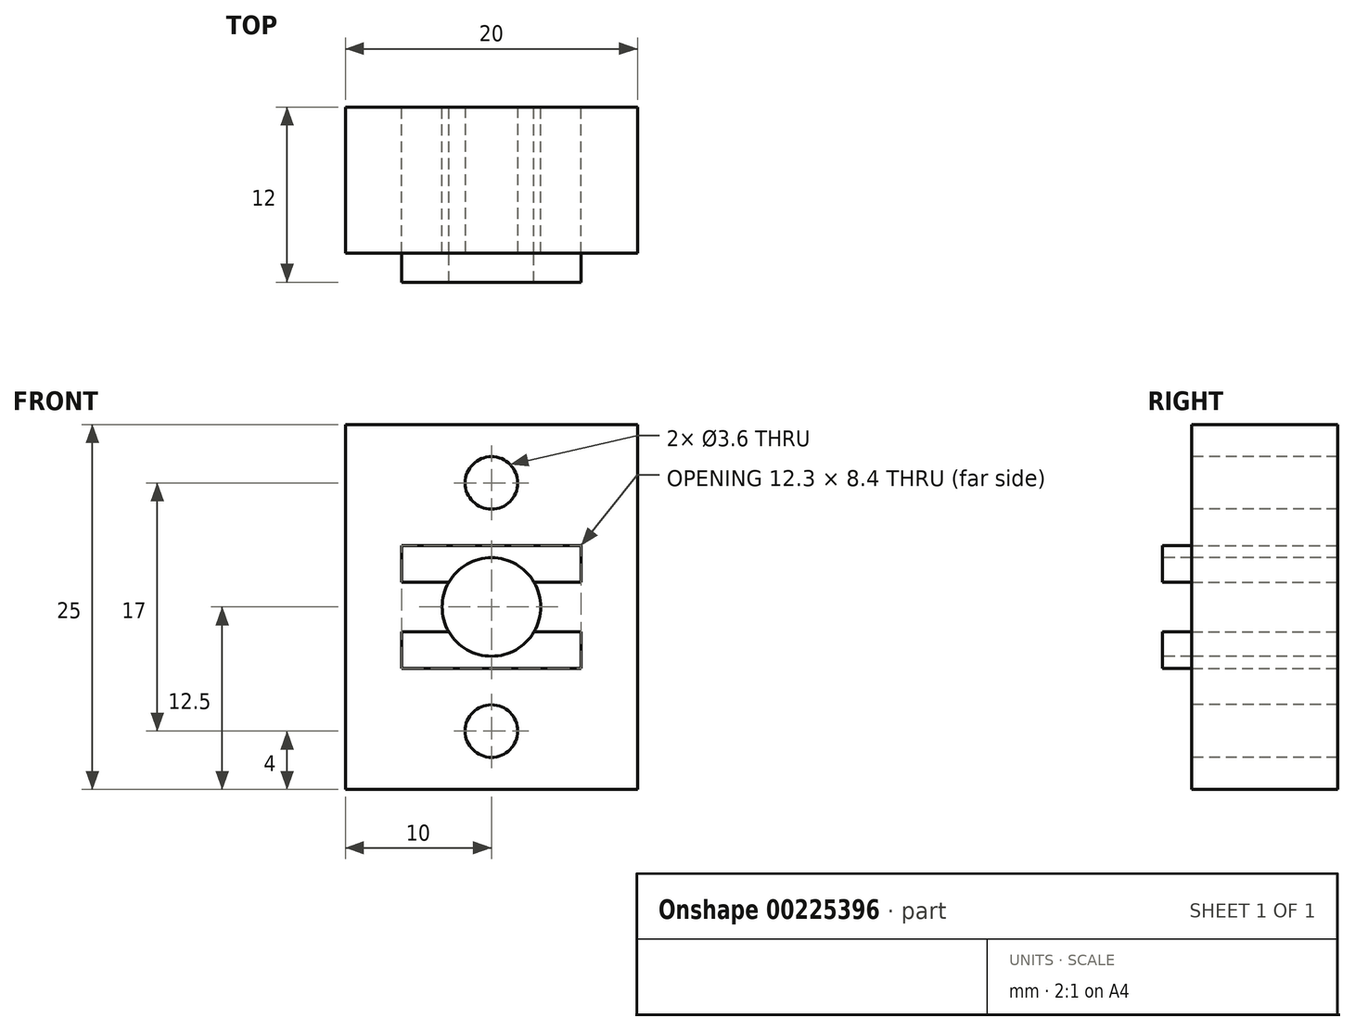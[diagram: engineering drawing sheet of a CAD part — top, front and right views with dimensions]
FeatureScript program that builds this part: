
annotation { "Feature Type Name" : "Feature", "Feature Type Description" : "" }
export const myFeature = defineFeature(function(context is Context, id is Id, definition is map)
    precondition{}
    {
        {
            var Q0;
            Q0=qCreatedBy(makeId("Front.planeOp"),FACE);
            var sketch = newSketch(context, id + "F0", { "sketchPlane" : qUnion([Q0])});
            skLineSegment(sketch, "E0.bottom", {"start": v(-5, 12.5) * mm, "end": v(5, 12.5) * mm, "construction": true});
            skLineSegment(sketch, "E0.top", {"start": v(-5, -12.5) * mm, "end": v(5, -12.5) * mm, "construction": true});
            skLineSegment(sketch, "E0.left", {"start": v(-5, 12.5) * mm, "end": v(-5, -12.5) * mm, "construction": true});
            skLineSegment(sketch, "E0.right", {"start": v(5, 12.5) * mm, "end": v(5, -12.5) * mm, "construction": true});
            skPoint(sketch, "E0.middle", {"position": v(0, 0) * mm});
            skCircle(sketch, "E1", {"center": v(5, 0) * mm, "radius": 3.17 * mm, "construction": true});
            skCircle(sketch, "E2", {"center": v(2.05, 2.95) * mm, "radius": 1 * mm, "construction": true});
            skCircle(sketch, "E3", {"center": v(2.05, -2.95) * mm, "radius": 1 * mm, "construction": true});
            skLineSegment(sketch, "E4", {"start": v(5, 0) * mm, "end": v(2.05, 2.95) * mm, "construction": true});
            skLineSegment(sketch, "E5", {"start": v(2.05, -2.95) * mm, "end": v(5, 0) * mm, "construction": true});
            skLineSegment(sketch, "E6.bottom", {"start": v(-1.15, 4.2) * mm, "end": v(3.25, 4.2) * mm, "construction": true});
            skLineSegment(sketch, "E6.top", {"start": v(-1.15, 1.7) * mm, "end": v(3.25, 1.7) * mm, "construction": true});
            skLineSegment(sketch, "E6.left", {"start": v(-1.15, 4.2) * mm, "end": v(-1.15, 1.7) * mm, "construction": true});
            skLineSegment(sketch, "E6.right", {"start": v(3.25, 4.2) * mm, "end": v(3.25, 1.7) * mm, "construction": true});
            skPoint(sketch, "E6.middle", {"position": v(1.05, 2.95) * mm});
            skLineSegment(sketch, "E7.MirrorCS", {"start": v(-1.15, -1.7) * mm, "end": v(3.25, -1.7) * mm, "construction": true});
            skLineSegment(sketch, "E8.MirrorCS", {"start": v(-1.15, -4.2) * mm, "end": v(-1.15, -1.7) * mm, "construction": true});
            skLineSegment(sketch, "E9.MirrorCS", {"start": v(-1.15, -4.2) * mm, "end": v(3.25, -4.2) * mm, "construction": true});
            skLineSegment(sketch, "E10.MirrorCS", {"start": v(3.25, -4.2) * mm, "end": v(3.25, -1.7) * mm, "construction": true});
            skLineSegment(sketch, "E11", {"start": v(-1.15, 4.2) * mm, "end": v(5, 4.2) * mm});
            skLineSegment(sketch, "E12", {"start": v(5, 12.5) * mm, "end": v(5, 4.2) * mm});
            skLineSegment(sketch, "E13", {"start": v(5, 12.5) * mm, "end": v(-5, 12.5) * mm});
            skLineSegment(sketch, "E14", {"start": v(-5, 12.5) * mm, "end": v(-5, -12.5) * mm});
            skLineSegment(sketch, "E15", {"start": v(-5, -12.5) * mm, "end": v(5, -12.5) * mm});
            skArc(sketch, "E16", {"start": v(2.09, 1.7) * mm, "mid": v(1.62, 0) * mm, "end": v(2.09, -1.7) * mm});
            skLineSegment(sketch, "E17", {"start": v(-1.15, 4.2) * mm, "end": v(-1.15, 1.7) * mm});
            skLineSegment(sketch, "E18", {"start": v(-1.15, 1.7) * mm, "end": v(2.09, 1.7) * mm});
            skLineSegment(sketch, "E19", {"start": v(-1.15, -1.7) * mm, "end": v(2.09, -1.7) * mm});
            skLineSegment(sketch, "E20", {"start": v(-1.15, -1.7) * mm, "end": v(-1.15, -4.2) * mm});
            skLineSegment(sketch, "E21", {"start": v(-1.15, -4.2) * mm, "end": v(5, -4.2) * mm});
            skLineSegment(sketch, "E22", {"start": v(5, -4.2) * mm, "end": v(5, -12.5) * mm});
            skCircle(sketch, "E23", {"center": v(0.05, 2.95) * mm, "radius": 1 * mm, "construction": true});
            skLineSegment(sketch, "E24", {"start": v(5, 0) * mm, "end": v(5, 15.82) * mm, "construction": true});
            skLineSegment(sketch, "E25", {"start": v(5, 15.82) * mm, "end": v(5, -17.9) * mm, "construction": true});
            skLineSegment(sketch, "E26.MirrorCS", {"start": v(11.15, 1.7) * mm, "end": v(7.91, 1.7) * mm});
            skLineSegment(sketch, "E27.MirrorCS", {"start": v(15, -12.5) * mm, "end": v(5, -12.5) * mm});
            skLineSegment(sketch, "E28.MirrorCS", {"start": v(5, 12.5) * mm, "end": v(15, 12.5) * mm});
            skLineSegment(sketch, "E29.MirrorCS", {"start": v(11.15, 4.2) * mm, "end": v(11.15, 1.7) * mm});
            skLineSegment(sketch, "E30.MirrorCS", {"start": v(15, 12.5) * mm, "end": v(15, -12.5) * mm});
            skLineSegment(sketch, "E31.MirrorCS", {"start": v(11.15, -1.7) * mm, "end": v(11.15, -4.2) * mm});
            skLineSegment(sketch, "E32.MirrorCS", {"start": v(11.15, -1.7) * mm, "end": v(7.91, -1.7) * mm});
            skLineSegment(sketch, "E33.MirrorCS", {"start": v(15, -12.5) * mm, "end": v(5, -12.5) * mm, "construction": true});
            skLineSegment(sketch, "E34.MirrorCS", {"start": v(11.15, -4.2) * mm, "end": v(6.75, -4.2) * mm, "construction": true});
            skLineSegment(sketch, "E35.MirrorCS", {"start": v(11.15, 4.2) * mm, "end": v(11.15, 1.7) * mm, "construction": true});
            skLineSegment(sketch, "E36.MirrorCS", {"start": v(6.75, -4.2) * mm, "end": v(6.75, -1.7) * mm, "construction": true});
            skLineSegment(sketch, "E37.MirrorCS", {"start": v(11.15, 4.2) * mm, "end": v(5, 4.2) * mm});
            skPoint(sketch, "E38.MirrorP", {"position": v(10, 0) * mm});
            skCircle(sketch, "E39.MirrorC", {"center": v(9.95, 2.95) * mm, "radius": 1 * mm, "construction": true});
            skLineSegment(sketch, "E40.MirrorCS", {"start": v(15, 12.5) * mm, "end": v(15, -12.5) * mm, "construction": true});
            skCircle(sketch, "E41.MirrorC", {"center": v(7.95, 2.95) * mm, "radius": 1 * mm, "construction": true});
            skLineSegment(sketch, "E42.MirrorCS", {"start": v(11.15, 1.7) * mm, "end": v(6.75, 1.7) * mm, "construction": true});
            skLineSegment(sketch, "E43.MirrorCS", {"start": v(11.15, -4.2) * mm, "end": v(11.15, -1.7) * mm, "construction": true});
            skCircle(sketch, "E44.MirrorC", {"center": v(7.95, -2.95) * mm, "radius": 1 * mm, "construction": true});
            skLineSegment(sketch, "E45.MirrorCS", {"start": v(11.15, -1.7) * mm, "end": v(6.75, -1.7) * mm, "construction": true});
            skArc(sketch, "E46.MirrorCS", {"start": v(7.91, 1.7) * mm, "mid": v(8.37, 0) * mm, "end": v(7.91, -1.7) * mm});
            skLineSegment(sketch, "E47.MirrorCS", {"start": v(6.75, 4.2) * mm, "end": v(6.75, 1.7) * mm, "construction": true});
            skLineSegment(sketch, "E48.MirrorCS", {"start": v(7.95, -2.95) * mm, "end": v(5, 0) * mm, "construction": true});
            skLineSegment(sketch, "E49.MirrorCS", {"start": v(11.15, -4.2) * mm, "end": v(5, -4.2) * mm});
            skPoint(sketch, "E50.MirrorP", {"position": v(8.95, 2.95) * mm});
            skLineSegment(sketch, "E51.MirrorCS", {"start": v(5, 0) * mm, "end": v(7.95, 2.95) * mm, "construction": true});
            skLineSegment(sketch, "E52.MirrorCS", {"start": v(15, 12.5) * mm, "end": v(5, 12.5) * mm, "construction": true});
            skLineSegment(sketch, "E53.MirrorCS", {"start": v(11.15, 4.2) * mm, "end": v(6.75, 4.2) * mm, "construction": true});
            skSolve(sketch);
        }
        {
            var Q0;
            Q0=makeQuery(id+"F0.imprint","IMPRINT",FACE,{"disambiguationData":[TD([[makeQuery(id+"F0.imprint","IMPRINT",EDGE,{"derivedFrom":sQuery(id+"F0.wireOp",EDGE,"E11")}),1.0]])]});
            var Q1;
            Q1=makeQuery(id+"F0.imprint","IMPRINT",FACE,{"disambiguationData":[TD([[makeQuery(id+"F0.imprint","IMPRINT",EDGE,{"derivedFrom":sQuery(id+"F0.wireOp",EDGE,"E26.MirrorCS")}),1.0]])]});
            extrude(context, id + "F1", {"entities" : qUnion([Q0, Q1]), "endBound" : BoundingType.SYMMETRIC, "offsetDistance" : 25 * mm, "depth" : 10 * mm});
        }
        {
            var Q0;
            Q0=makeQuery(id+"F1.opExtrude","CAP_FACE",FACE,{"disambiguationData":[OSD([sQuery(id+"F0.wireOp",EDGE,"E11"),sQuery(id+"F0.wireOp",EDGE,"E13"),sQuery(id+"F0.wireOp",EDGE,"E14"),sQuery(id+"F0.wireOp",EDGE,"E15"),sQuery(id+"F0.wireOp",EDGE,"E16"),sQuery(id+"F0.wireOp",EDGE,"E17"),sQuery(id+"F0.wireOp",EDGE,"E18"),sQuery(id+"F0.wireOp",EDGE,"E19"),sQuery(id+"F0.wireOp",EDGE,"E20"),sQuery(id+"F0.wireOp",EDGE,"E21"),sQuery(id+"F0.wireOp",EDGE,"E26.MirrorCS"),sQuery(id+"F0.wireOp",EDGE,"E27.MirrorCS"),sQuery(id+"F0.wireOp",EDGE,"E28.MirrorCS"),sQuery(id+"F0.wireOp",EDGE,"E29.MirrorCS"),sQuery(id+"F0.wireOp",EDGE,"E30.MirrorCS"),sQuery(id+"F0.wireOp",EDGE,"E31.MirrorCS"),sQuery(id+"F0.wireOp",EDGE,"E32.MirrorCS"),sQuery(id+"F0.wireOp",EDGE,"E37.MirrorCS"),sQuery(id+"F0.wireOp",EDGE,"E46.MirrorCS"),sQuery(id+"F0.wireOp",EDGE,"E49.MirrorCS")])],"isStart":false});
            var sketch = newSketch(context, id + "F2", { "sketchPlane" : qUnion([Q0])});
            skPoint(sketch, "E54", {"position": v(5, 8.5) * mm});
            skPoint(sketch, "E54.positionSnap0", {"position": v(5, 4.2) * mm});
            skPoint(sketch, "E55", {"position": v(5, -8.5) * mm});
            skSolve(sketch);
        }
        {
            var Q0;
            Q0=sQuery(id+"F2.wireOp",VERTEX,"E54");
            var Q1;
            Q1=sQuery(id+"F2.wireOp",VERTEX,"E55");
            var Q2;
            Q2=makeQuery(id+"F1.opExtrude","SWEPT_BODY",BODY,{"disambiguationData":[OSD([sQuery(id+"F0.wireOp",EDGE,"E11"),sQuery(id+"F0.wireOp",EDGE,"E13"),sQuery(id+"F0.wireOp",EDGE,"E14"),sQuery(id+"F0.wireOp",EDGE,"E15"),sQuery(id+"F0.wireOp",EDGE,"E16"),sQuery(id+"F0.wireOp",EDGE,"E17"),sQuery(id+"F0.wireOp",EDGE,"E18"),sQuery(id+"F0.wireOp",EDGE,"E19"),sQuery(id+"F0.wireOp",EDGE,"E20"),sQuery(id+"F0.wireOp",EDGE,"E21"),sQuery(id+"F0.wireOp",EDGE,"E26.MirrorCS"),sQuery(id+"F0.wireOp",EDGE,"E27.MirrorCS"),sQuery(id+"F0.wireOp",EDGE,"E28.MirrorCS"),sQuery(id+"F0.wireOp",EDGE,"E29.MirrorCS"),sQuery(id+"F0.wireOp",EDGE,"E30.MirrorCS"),sQuery(id+"F0.wireOp",EDGE,"E31.MirrorCS"),sQuery(id+"F0.wireOp",EDGE,"E32.MirrorCS"),sQuery(id+"F0.wireOp",EDGE,"E37.MirrorCS"),sQuery(id+"F0.wireOp",EDGE,"E46.MirrorCS"),sQuery(id+"F0.wireOp",EDGE,"E49.MirrorCS")])]});
            hole(context, id + "F3", {"style" : HoleStyle.SIMPLE, "endStyle" : HoleEndStyle.BLIND, "standardTappedOrClearance" : lookupTablePath({ "fit" : "Loose", "standard" : "ISO", "size" : "M3", "type" : "Clearance" }), "standardBlindInLast" : lookupTablePath({ "fit" : "Loose", "standard" : "ISO", "engagement" : "75%", "pitch" : "0.5 mm", "size" : "M3", "type" : "Clearance & tapped" }), "holeDiameter" : 3.6 * mm, "majorDiameter" : 5 * mm, "holeDepth" : 35 * mm, "isTappedThrough" : true, "tappedDepth" : 12 * mm, "tapClearance" : 3, "startFromSketch" : true, "locations" : qUnion([Q0, Q1]), "scope" : qUnion([Q2])});
        }
        {
            var Q0;
            Q0=makeQuery(id+"F1.opExtrude","CAP_FACE",FACE,{"disambiguationData":[OSD([sQuery(id+"F0.wireOp",EDGE,"E11"),sQuery(id+"F0.wireOp",EDGE,"E13"),sQuery(id+"F0.wireOp",EDGE,"E14"),sQuery(id+"F0.wireOp",EDGE,"E15"),sQuery(id+"F0.wireOp",EDGE,"E16"),sQuery(id+"F0.wireOp",EDGE,"E17"),sQuery(id+"F0.wireOp",EDGE,"E18"),sQuery(id+"F0.wireOp",EDGE,"E19"),sQuery(id+"F0.wireOp",EDGE,"E20"),sQuery(id+"F0.wireOp",EDGE,"E21"),sQuery(id+"F0.wireOp",EDGE,"E26.MirrorCS"),sQuery(id+"F0.wireOp",EDGE,"E27.MirrorCS"),sQuery(id+"F0.wireOp",EDGE,"E28.MirrorCS"),sQuery(id+"F0.wireOp",EDGE,"E29.MirrorCS"),sQuery(id+"F0.wireOp",EDGE,"E30.MirrorCS"),sQuery(id+"F0.wireOp",EDGE,"E31.MirrorCS"),sQuery(id+"F0.wireOp",EDGE,"E32.MirrorCS"),sQuery(id+"F0.wireOp",EDGE,"E37.MirrorCS"),sQuery(id+"F0.wireOp",EDGE,"E46.MirrorCS"),sQuery(id+"F0.wireOp",EDGE,"E49.MirrorCS")])],"isStart":false});
            var sketch = newSketch(context, id + "F4", { "sketchPlane" : qUnion([Q0])});
            skLineSegment(sketch, "E56.0.0", {"start": v(-5, -12.5) * mm, "end": v(15, -12.5) * mm});
            skLineSegment(sketch, "E56.0.1", {"start": v(15, -12.5) * mm, "end": v(15, 12.5) * mm});
            skLineSegment(sketch, "E56.0.2", {"start": v(15, 12.5) * mm, "end": v(-5, 12.5) * mm});
            skLineSegment(sketch, "E56.0.3", {"start": v(-5, 12.5) * mm, "end": v(-5, -12.5) * mm});
            skSolve(sketch);
        }
        {
            var Q0;
            Q0=makeQuery(id+"F4.imprint","IMPRINT",FACE,{"disambiguationData":[TD([[makeQuery(id+"F4.imprint","IMPRINT",EDGE,{"derivedFrom":makeQuery(id+"F1.opExtrude","CAP_EDGE",EDGE,{"disambiguationData":[OSD([sQuery(id+"F0.wireOp",EDGE,"E16")])],"isStart":false})}),1.0]])]});
            extrude(context, id + "F5", {"entities" : qUnion([Q0]), "depth" : 2 * mm, "offsetDistance" : 25 * mm});
        }
        {
            var Q0;
            Q0=makeQuery(id+"F1.opExtrude","CAP_FACE",FACE,{"disambiguationData":[OSD([sQuery(id+"F0.wireOp",EDGE,"E11"),sQuery(id+"F0.wireOp",EDGE,"E13"),sQuery(id+"F0.wireOp",EDGE,"E14"),sQuery(id+"F0.wireOp",EDGE,"E15"),sQuery(id+"F0.wireOp",EDGE,"E16"),sQuery(id+"F0.wireOp",EDGE,"E17"),sQuery(id+"F0.wireOp",EDGE,"E18"),sQuery(id+"F0.wireOp",EDGE,"E19"),sQuery(id+"F0.wireOp",EDGE,"E20"),sQuery(id+"F0.wireOp",EDGE,"E21"),sQuery(id+"F0.wireOp",EDGE,"E26.MirrorCS"),sQuery(id+"F0.wireOp",EDGE,"E27.MirrorCS"),sQuery(id+"F0.wireOp",EDGE,"E28.MirrorCS"),sQuery(id+"F0.wireOp",EDGE,"E29.MirrorCS"),sQuery(id+"F0.wireOp",EDGE,"E30.MirrorCS"),sQuery(id+"F0.wireOp",EDGE,"E31.MirrorCS"),sQuery(id+"F0.wireOp",EDGE,"E32.MirrorCS"),sQuery(id+"F0.wireOp",EDGE,"E37.MirrorCS"),sQuery(id+"F0.wireOp",EDGE,"E46.MirrorCS"),sQuery(id+"F0.wireOp",EDGE,"E49.MirrorCS")])],"isStart":true});
            var sketch = newSketch(context, id + "F6", { "sketchPlane" : qUnion([Q0])});
            skLineSegment(sketch, "E57.0.0", {"start": v(-15, -12.5) * mm, "end": v(5, -12.5) * mm});
            skLineSegment(sketch, "E57.0.1", {"start": v(5, -12.5) * mm, "end": v(5, 12.5) * mm});
            skLineSegment(sketch, "E57.0.2", {"start": v(5, 12.5) * mm, "end": v(-15, 12.5) * mm});
            skLineSegment(sketch, "E57.0.3", {"start": v(-15, 12.5) * mm, "end": v(-15, -12.5) * mm});
            skSolve(sketch);
        }
        {
            var Q0;
            Q0=makeQuery(id+"F6.imprint","IMPRINT",FACE,{"disambiguationData":[TD([[makeQuery(id+"F6.imprint","IMPRINT",EDGE,{"derivedFrom":makeQuery(id+"F1.opExtrude","CAP_EDGE",EDGE,{"disambiguationData":[OSD([sQuery(id+"F0.wireOp",EDGE,"E16")])],"isStart":true})}),-1.0]])]});
            var Q1;
            Q1=makeQuery(id+"F5.opExtrude","CAP_FACE",FACE,{"disambiguationData":[OSD([sQuery(id+"F0.wireOp",EDGE,"E11"),sQuery(id+"F0.wireOp",EDGE,"E16"),sQuery(id+"F0.wireOp",EDGE,"E17"),sQuery(id+"F0.wireOp",EDGE,"E18"),sQuery(id+"F0.wireOp",EDGE,"E19"),sQuery(id+"F0.wireOp",EDGE,"E20"),sQuery(id+"F0.wireOp",EDGE,"E21"),sQuery(id+"F0.wireOp",EDGE,"E26.MirrorCS"),sQuery(id+"F0.wireOp",EDGE,"E29.MirrorCS"),sQuery(id+"F0.wireOp",EDGE,"E31.MirrorCS"),sQuery(id+"F0.wireOp",EDGE,"E32.MirrorCS"),sQuery(id+"F0.wireOp",EDGE,"E37.MirrorCS"),sQuery(id+"F0.wireOp",EDGE,"E46.MirrorCS"),sQuery(id+"F0.wireOp",EDGE,"E49.MirrorCS")])],"isStart":true});
            extrude(context, id + "F7", {"entities" : qUnion([Q0]), "depth" : 0 * mm, "offsetDistance" : 25 * mm, "hasSecondDirection" : true, "secondDirectionBound" : SecondDirectionBoundingType.UP_TO_SURFACE, "secondDirectionOppositeDirection" : true, "secondDirectionDepth" : 25 * mm, "secondDirectionBoundEntityFace" : qUnion([Q1])});
        }
        {
            var Q0;
            Q0=makeQuery(id+"F5.opExtrude","CAP_FACE",FACE,{"disambiguationData":[OSD([sQuery(id+"F0.wireOp",EDGE,"E11"),sQuery(id+"F0.wireOp",EDGE,"E16"),sQuery(id+"F0.wireOp",EDGE,"E17"),sQuery(id+"F0.wireOp",EDGE,"E18"),sQuery(id+"F0.wireOp",EDGE,"E19"),sQuery(id+"F0.wireOp",EDGE,"E20"),sQuery(id+"F0.wireOp",EDGE,"E21"),sQuery(id+"F0.wireOp",EDGE,"E26.MirrorCS"),sQuery(id+"F0.wireOp",EDGE,"E29.MirrorCS"),sQuery(id+"F0.wireOp",EDGE,"E31.MirrorCS"),sQuery(id+"F0.wireOp",EDGE,"E32.MirrorCS"),sQuery(id+"F0.wireOp",EDGE,"E37.MirrorCS"),sQuery(id+"F0.wireOp",EDGE,"E46.MirrorCS"),sQuery(id+"F0.wireOp",EDGE,"E49.MirrorCS")])],"isStart":false});
            var sketch = newSketch(context, id + "F8", { "sketchPlane" : qUnion([Q0])});
            skLineSegment(sketch, "E58.0.0", {"start": v(11.15, -4.2) * mm, "end": v(11.15, -1.7) * mm});
            skLineSegment(sketch, "E58.0.1", {"start": v(11.15, -1.7) * mm, "end": v(7.91, -1.7) * mm});
            skArc(sketch, "E58.0.2", {"start": v(7.91, -1.7) * mm, "mid": v(8.37, 0) * mm, "end": v(7.91, 1.7) * mm});
            skLineSegment(sketch, "E58.0.3", {"start": v(7.91, 1.7) * mm, "end": v(11.15, 1.7) * mm});
            skLineSegment(sketch, "E58.0.4", {"start": v(11.15, 1.7) * mm, "end": v(11.15, 4.2) * mm});
            skLineSegment(sketch, "E58.0.5", {"start": v(11.15, 4.2) * mm, "end": v(-1.15, 4.2) * mm});
            skLineSegment(sketch, "E58.0.6", {"start": v(-1.15, 4.2) * mm, "end": v(-1.15, 1.7) * mm});
            skLineSegment(sketch, "E58.0.7", {"start": v(-1.15, 1.7) * mm, "end": v(2.09, 1.7) * mm});
            skArc(sketch, "E58.0.8", {"start": v(2.09, 1.7) * mm, "mid": v(1.62, 0) * mm, "end": v(2.09, -1.7) * mm});
            skLineSegment(sketch, "E58.0.9", {"start": v(2.09, -1.7) * mm, "end": v(-1.15, -1.7) * mm});
            skLineSegment(sketch, "E58.0.10", {"start": v(-1.15, -1.7) * mm, "end": v(-1.15, -4.2) * mm});
            skLineSegment(sketch, "E58.0.11", {"start": v(-1.15, -4.2) * mm, "end": v(11.15, -4.2) * mm});
            skCircle(sketch, "E59", {"center": v(5, 0) * mm, "radius": 3.37 * mm});
            skSolve(sketch);
        }
        {
            var Q0;
            {var subQ4=sQuery(id+"F8.wireOp",EDGE,"E58.0.8");Q0=makeQuery(id+"F8.imprint","IMPRINT",FACE,{"disambiguationData":[TD([[makeQuery(id+"F8.imprint","IMPRINT",EDGE,{"derivedFrom":subQ4}),1.0]])]});}
            extrude(context, id + "F9", {"entities" : qUnion([Q0]), "operationType" : NewBodyOperationType.REMOVE, "endBound" : BoundingType.THROUGH_ALL, "oppositeDirection" : true, "depth" : 25 * mm, "offsetDistance" : 25 * mm});
        }
    });
